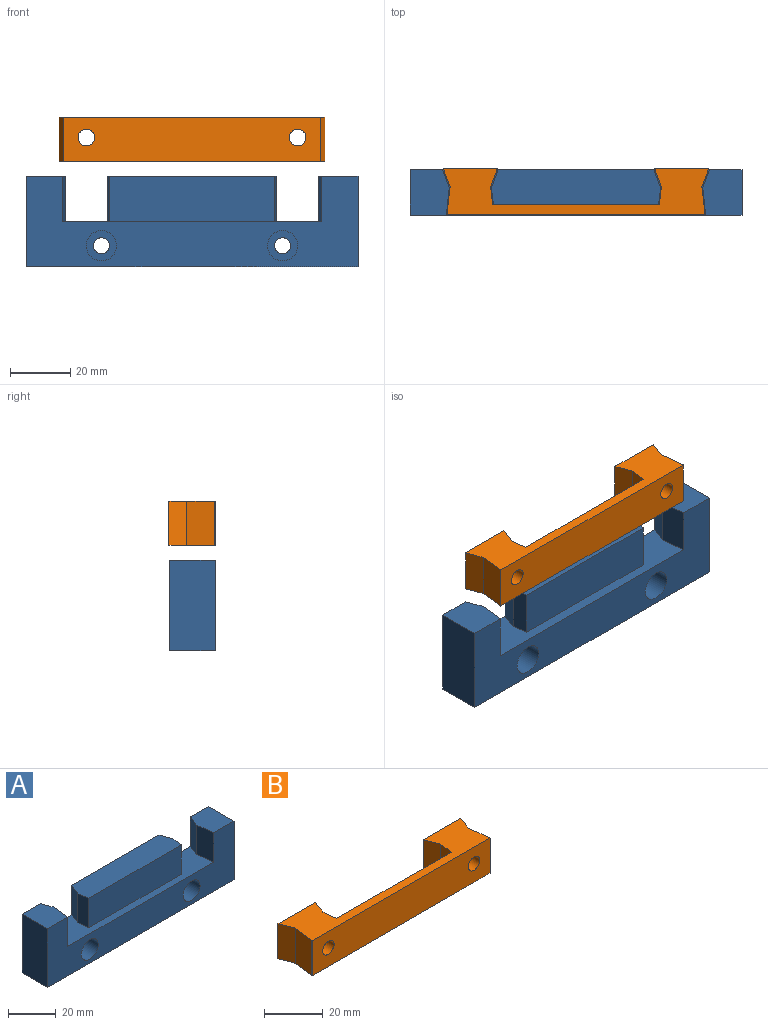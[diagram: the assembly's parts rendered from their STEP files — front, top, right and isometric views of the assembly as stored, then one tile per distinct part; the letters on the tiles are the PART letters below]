
ASSEMBLY  parts=2 mates=1
PART A: 24 faces, bbox 110x15x30 mm
  f0: plane 30x15mm, normal (1,0,0), area 450mm2, adj f3,f4,f6,f23
  f1: plane 15x13mm, normal (0,0,1), area 183.8mm2, adj f4,f5,f8,f9,f23
  f2: plane 56x11.6mm, normal (0,0,1), area 632.6mm2, adj f7,f12,f13,f14,f15,f23
  f3: plane 15x13mm, normal (0,0,1), area 183.7mm2, adj f0,f4,f10,f11,f23
  f4: plane 110x30mm, normal (0,-1,0), area 1852.9mm2, adj f0,f1,f3,f5,f6,f9,f10,f16
  f5: plane 30x15mm, normal (-1,0,0), area 450mm2, adj f1,f4,f6,f23
  f6: plane 110x15mm, normal (0,0,-1), area 1650mm2, adj f0,f4,f5,f23
  f7: plane 15x6mm, normal (-0.94,0.35,0), area 96.1mm2, adj f2,f15,f16,f23
  f8: plane 15x6mm, normal (0.94,0.35,0), area 96.1mm2, adj f1,f9,f16,f23
  f9: plane 15x9mm, normal (0.99,-0.11,0), area 135.8mm2, adj f1,f4,f8,f16
  f10: plane 15x9mm, normal (-0.99,-0.11,0), area 135.8mm2, adj f3,f4,f11,f16
  f11: plane 15x6mm, normal (-0.94,0.35,0), area 96.1mm2, adj f3,f10,f16,f23
  f12: plane 15x6mm, normal (0.94,0.35,0), area 96.1mm2, adj f2,f13,f16,f23
  f13: plane 15x5.6mm, normal (0.99,-0.11,0), area 84.5mm2, adj f2,f12,f14,f16
  f14: plane 54.76x15mm, normal (0,-1,0), area 821.3mm2, adj f2,f13,f15,f16
  f15: plane 15x5.6mm, normal (-0.99,-0.11,0), area 84.5mm2, adj f2,f7,f14,f16
  f16: plane 88.5x15mm, normal (0,0,1), area 649.9mm2, adj f4,f7,f8,f9,f10,f11,f12,f13
  f17: cylinder r=2.65mm len=5.3mm, axis (0,-1,0), area 83.3mm2, adj f18,f23
  f18: plane 10x10mm, normal (0,-1,0), area 56.5mm2, adj f17,f19
  f19: cylinder r=5mm len=10mm, axis (0,-1,0), area 314.2mm2, adj f4,f18
  f20: cylinder r=2.65mm len=5.3mm, axis (0,-1,0), area 83.3mm2, adj f21,f23
  f21: plane 10x10mm, normal (0,-1,0), area 56.5mm2, adj f20,f22
  f22: cylinder r=5mm len=10mm, axis (0,-1,0), area 314.2mm2, adj f4,f21
  f23: plane 110x30mm, normal (0,1,0), area 2700.9mm2, adj f0,f1,f2,f3,f5,f6,f7,f8
PART B: 32 faces, bbox 87.9x15.3x14.6 mm
  f0: plane 87.89x15.3mm, normal (0,0,1), area 644.1mm2, adj f1,f2,f3,f4,f5,f6,f7,f8
  f1: plane 14.6x9.04mm, normal (0.99,0.11,0), area 132.7mm2, adj f0,f3,f10,f12
  f2: plane 14.6x9.04mm, normal (-0.99,0.11,0), area 132.7mm2, adj f0,f9,f10,f11
  f3: plane 14.6x5.96mm, normal (0.94,-0.35,0), area 93mm2, adj f0,f1,f10,f30
  f4: plane 14.6x5.96mm, normal (-0.94,-0.35,0), area 93mm2, adj f0,f5,f10,f30
  f5: plane 14.6x5.92mm, normal (-0.99,0.11,0), area 87mm2, adj f0,f4,f6,f10
  f6: plane 55.27x14.6mm, normal (0,1,0), area 806.9mm2, adj f0,f5,f7,f10
  f7: plane 14.6x5.92mm, normal (0.99,0.11,0), area 87mm2, adj f0,f6,f8,f10
  f8: plane 14.6x5.96mm, normal (0.94,-0.35,0), area 93mm2, adj f0,f7,f10,f31
  f9: plane 14.6x5.96mm, normal (-0.94,-0.35,0), area 93mm2, adj f0,f2,f10,f31
  f10: plane 87.89x15.3mm, normal (0,0,-1), area 644.1mm2, adj f1,f2,f3,f4,f5,f6,f7,f8
  f11: plane 14.6x0.3mm, normal (-1,0,0), area 4.4mm2, adj f0,f2,f10,f13
  f12: plane 14.6x0.3mm, normal (1,0,0), area 4.4mm2, adj f0,f1,f10,f13
  f13: plane 85.43x14.6mm, normal (0,-1,0), area 1199.7mm2, adj f0,f10,f11,f12,f28,f29
  f14: plane 6.29x4.27mm, normal (-0.87,0,0.5), area 31mm2, adj f15,f19,f20,f31
  f15: plane 6.29x4.92mm, normal (0,0,1), area 31mm2, adj f14,f16,f20,f31
  f16: plane 6.29x4.27mm, normal (0.87,0,0.5), area 31mm2, adj f15,f17,f20,f31
  f17: plane 6.29x4.27mm, normal (0.87,0,-0.5), area 31mm2, adj f16,f18,f20,f31
  f18: plane 6.29x4.92mm, normal (0,0,-1), area 31mm2, adj f17,f19,f20,f31
  f19: plane 6.29x4.27mm, normal (-0.87,0,-0.5), area 31mm2, adj f14,f18,f20,f31
  f20: plane 9.85x8.53mm, normal (0,1,0), area 39.3mm2, adj f14,f15,f16,f17,f18,f19,f29
  f21: plane 6.29x4.27mm, normal (0.87,0,-0.5), area 31mm2, adj f22,f26,f27,f30
  f22: plane 6.29x4.92mm, normal (0,0,-1), area 31mm2, adj f21,f23,f27,f30
  f23: plane 6.29x4.27mm, normal (-0.87,0,-0.5), area 31mm2, adj f22,f24,f27,f30
  f24: plane 6.29x4.27mm, normal (-0.87,0,0.5), area 31mm2, adj f23,f25,f27,f30
  f25: plane 6.29x4.92mm, normal (0,0,1), area 31mm2, adj f24,f26,f27,f30
  f26: plane 6.29x4.27mm, normal (0.87,0,0.5), area 31mm2, adj f21,f25,f27,f30
  f27: plane 9.85x8.53mm, normal (0,1,0), area 39.3mm2, adj f21,f22,f23,f24,f25,f26,f28
  f28: cylinder r=2.75mm len=9.02mm, axis (0,1,0), area 155.8mm2, adj f13,f27
  f29: cylinder r=2.75mm len=9.02mm, axis (0,1,0), area 155.8mm2, adj f13,f20
  f30: plane 17.89x14.6mm, normal (0,1,0), area 198.2mm2, adj f0,f3,f4,f10,f21,f22,f23,f24
  f31: plane 17.89x14.6mm, normal (0,1,0), area 198.2mm2, adj f0,f8,f9,f10,f14,f15,f16,f17
PLACE A t=(-8.26,15.42,-13.83)mm fixed
PLACE B t=(-8.26,15.72,5.77)mm
MATE slider B.f10 <-> A.f16  axis (0,0,-1) through (46.74,15.42,21.17)mm
